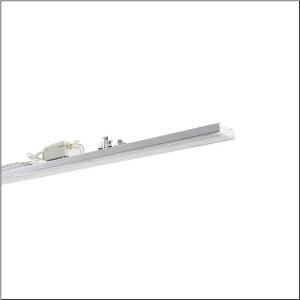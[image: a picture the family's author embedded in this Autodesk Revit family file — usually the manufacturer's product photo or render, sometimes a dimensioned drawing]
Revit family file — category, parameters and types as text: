
# Revit family: licross_21_recessed_mo_52te11dv4fxg
name_source: partatom
category: Lighting Fixtures
units: mm (PartAtom-declared; Revit-internal decimal feet)

## family parameters
Cut with Voids When Loaded = No
Host = Face
Light Source = No
Part Type = Normal
Room Calculation Point = No
Round Connector Dimension = Use Diameter
Shared = No

## types (1)
- --- (1 x LED, 15180 lm, 85.3 W, 4000K)
    Apparent Load = 85 VA
    CIE Flux Codes = 89 96 99 100 100
    Color Rendering = 80
    Color Temperature = 4000K
    Default Elevation = 1800 mm
    Description = Licross 21 Recessed MO, luminaire insert, of sheet steel, galvanised, coil coated, white, length: 2.250mm, width: 66mm, height: 67mm, LED rated luminous flux: 15.180lm, light colour: 840, SDCM (Standard Deviation of Colour Matching)MacAdam ≤ 3 SDCM (initial), control gear: DALI 2, with plug, 5-pole, with phase selection, mains connection: 220..240V, AC, 50/60Hz, rated input power: 85W, internal wiring halogen-free, primary light control with lens, of plastic, primary optical cover: cover, of PMMA, light emission: direct distribution, primary light characteristic: symmetric, protection rating (complete): IP54, insulation class (complete): insulation class I (protective earthing), certification: CE, ENEC, VDE, UKCA, protection symbol: D if used in an environment with non-conductive dust loads with corresponding accessories, impact resistance: IK06, permissible ambient temperature for indoor applications: -25..+35°C, corresponds to IFS (International Featured Standards) requirements for safety and quality in the food industry, reducing of maximum allowable ambient temperature of 5°C with ceiling mounting, LABS conformity tested according to VDMA 24364:2018-05, The light source and the operating device comply with the requirements of the Ecodesign Regulation (EU) 2019/2020 and are replaceable in accordance with this regulation, packaging unit: 1 piece
    Height = 58 mm
    Lamp = 1 x LED
    Lamp Light Flux = 15180 lm
    Lamp Power = 85.3 W
    Lamp count = 1
    Length = 2250 mm
    Luminous efficacy = 178 lm/W
    Manufacturer = Siteco
    ModVariant = No
    Model = 52TE11DV4FXG
    Mounting Place = Ceiling
    Mounting Type = Pendant
    Number of Poles = 1
    OnlyDefault = Yes
    Power Factor = 1
    Product Name = Licross 21 Recessed MO
    Product group = luminaire insert | ceiling pendant
    ProductGroupID = 901
    Protection Class = Protection class I
    Protection Degree = IP 54
    RLX_Detail_Level = 1
    RLX_Emergency_Light_Flux = 0 lm
    RLX_Emergency_Type = 0
    RLX_Emergency_Type_DB = No
    RlxData = <blob elided: 29709 chars, md5=8e09251e>
    Socket = socket
    Standby Power = 0 W
    System Light Flux = 15180 lm
    System Power = 85 W
    Type Comments = factory setting: luminous flux: 100 % | dim-lin: 254 | 390 mA
    Type Image = l_1296930.jpg
    URL = http://relux.com
    VarID = @adj_128773
    Voltage = 0 V
    Weight = 0.00 kg
    Width = 66 mm

## geometry (parser evidence)
native form markers: Blend x4, Sweep x10
no freeform markers — native parametric forms only
